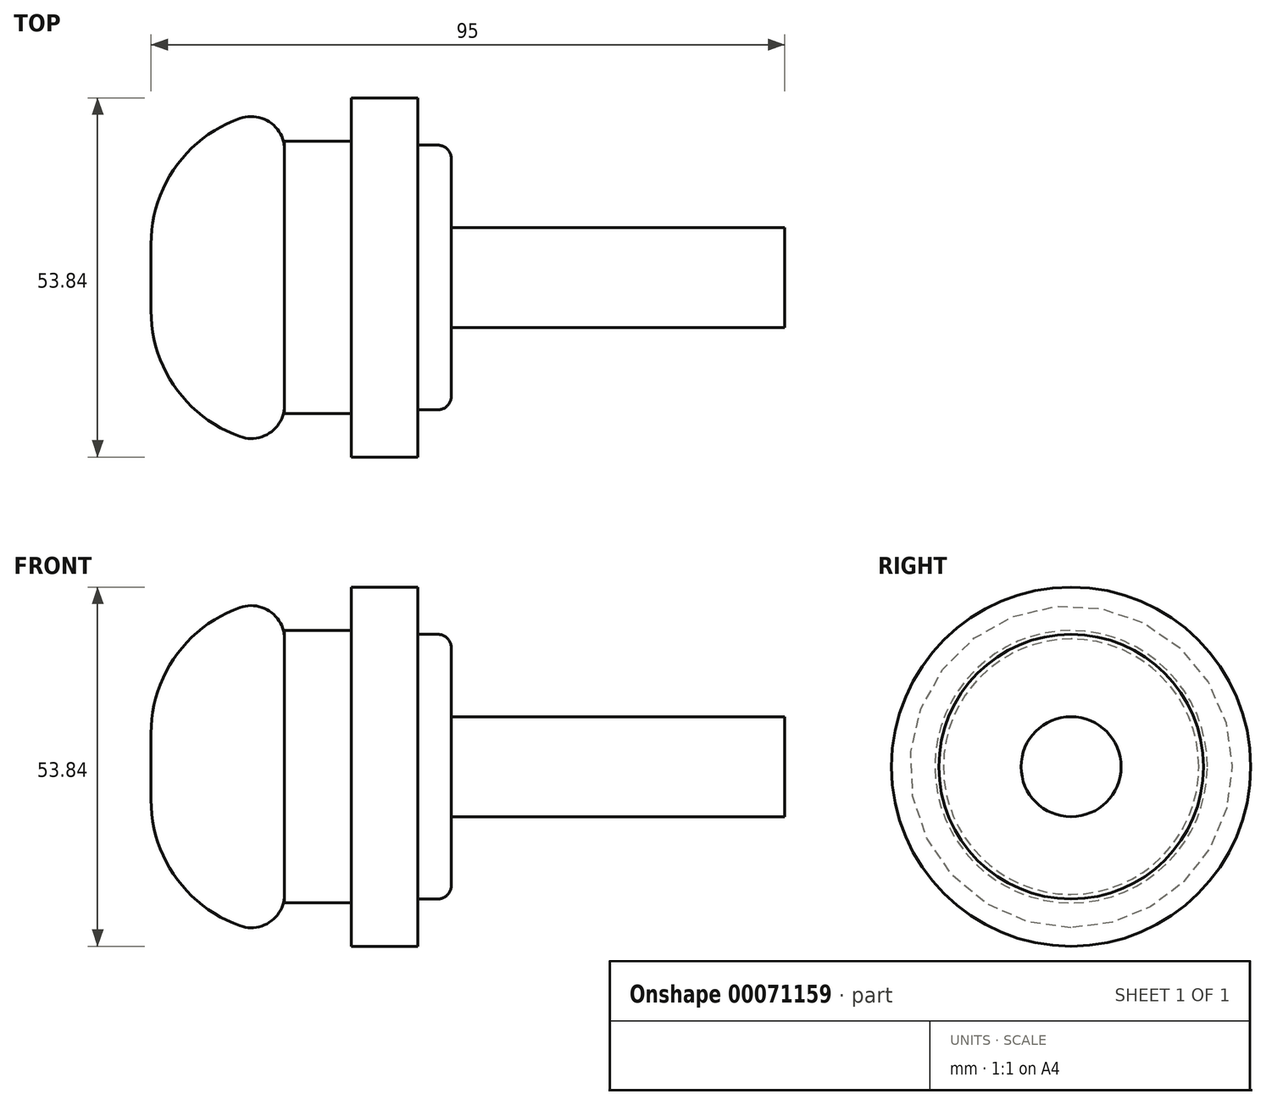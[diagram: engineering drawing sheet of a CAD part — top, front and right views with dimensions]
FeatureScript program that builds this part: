
annotation { "Feature Type Name" : "Feature", "Feature Type Description" : "" }
export const myFeature = defineFeature(function(context is Context, id is Id, definition is map)
    precondition{}
    {
        {
            var Q0;
            Q0=qCreatedBy(makeId("Right.planeOp"),FACE);
            var sketch = newSketch(context, id + "F0", { "sketchPlane" : qUnion([Q0])});
            skCircle(sketch, "E0", {"center": v(0, 0) * mm, "radius": 25 * mm});
            skSolve(sketch);
        }
        {
            var Q0;
            Q0 = qSketchRegion(id + "F0", true);
            extrude(context, id + "F1", {"entities" : qUnion([Q0]), "depth" : 20 * mm});
        }
        {
            var Q0;
            Q0=makeQuery(id+"F1.opExtrude","CAP_EDGE",EDGE,{"disambiguationData":[OSD([sQuery(id+"F0.wireOp",EDGE,"E0")])],"isStart":true});
            fillet(context, id + "F2", {"entities" : qUnion([Q0]), "radius" : 20 * mm, "tangentPropagation" : true, "allowEdgeOverflow" : false});
        }
        {
            var Q0;
            Q0=makeQuery(id+"F1.opExtrude","CAP_FACE",FACE,{"disambiguationData":[OSD([sQuery(id+"F0.wireOp",EDGE,"E0")])],"isStart":false});
            fillet(context, id + "F3", {"entities" : qUnion([Q0]), "radius" : 5 * mm, "tangentPropagation" : true, "allowEdgeOverflow" : false});
        }
        {
            var Q0;
            Q0=makeQuery(id+"F1.opExtrude","CAP_FACE",FACE,{"disambiguationData":[OSD([sQuery(id+"F0.wireOp",EDGE,"E0")])],"isStart":false});
            var sketch = newSketch(context, id + "F4", { "sketchPlane" : qUnion([Q0])});
            skCircle(sketch, "E1", {"center": v(0, 0) * mm, "radius": 20.42 * mm});
            skSolve(sketch);
        }
        {
            var Q0;
            Q0 = qSketchRegion(id + "F4", true);
            extrude(context, id + "F5", {"entities" : qUnion([Q0]), "operationType" : NewBodyOperationType.ADD, "depth" : 10 * mm});
        }
        {
            var Q0;
            Q0=makeQuery(id+"F5.opExtrude","CAP_FACE",FACE,{"disambiguationData":[OSD([sQuery(id+"F4.wireOp",EDGE,"E1")])],"isStart":false});
            var sketch = newSketch(context, id + "F6", { "sketchPlane" : qUnion([Q0])});
            skCircle(sketch, "E2", {"center": v(0, 0) * mm, "radius": 26.92 * mm});
            skSolve(sketch);
        }
        {
            var Q0;
            Q0 = qSketchRegion(id + "F6", true);
            extrude(context, id + "F7", {"entities" : qUnion([Q0]), "operationType" : NewBodyOperationType.ADD, "depth" : 10 * mm});
        }
        {
            var Q0;
            Q0=makeQuery(id+"F7.opExtrude","CAP_FACE",FACE,{"disambiguationData":[OSD([sQuery(id+"F6.wireOp",EDGE,"E2")])],"isStart":false});
            var sketch = newSketch(context, id + "F8", { "sketchPlane" : qUnion([Q0])});
            skCircle(sketch, "E3", {"center": v(0, 0) * mm, "radius": 19.84 * mm});
            skSolve(sketch);
        }
        {
            var Q0;
            Q0=makeQuery(id+"F8.imprint","IMPRINT",FACE,{"disambiguationData":[TD([[makeQuery(id+"F8.imprint","IMPRINT",EDGE,{"derivedFrom":sQuery(id+"F8.wireOp",EDGE,"E3")}),1.0]])]});
            extrude(context, id + "F9", {"entities" : qUnion([Q0]), "operationType" : NewBodyOperationType.ADD, "depth" : 5 * mm});
        }
        {
            var Q0;
            Q0=makeQuery(id+"F9.opExtrude","CAP_EDGE",EDGE,{"disambiguationData":[OSD([sQuery(id+"F8.wireOp",EDGE,"E3")])],"isStart":false});
            fillet(context, id + "F10", {"entities" : qUnion([Q0]), "radius" : 2 * mm, "tangentPropagation" : true, "allowEdgeOverflow" : false});
        }
        {
            var Q0;
            Q0=makeQuery(id+"F9.opExtrude","CAP_FACE",FACE,{"disambiguationData":[OSD([sQuery(id+"F8.wireOp",EDGE,"E3")])],"isStart":false});
            var sketch = newSketch(context, id + "F11", { "sketchPlane" : qUnion([Q0])});
            skCircle(sketch, "E4", {"center": v(0, 0) * mm, "radius": 7.5 * mm});
            skSolve(sketch);
        }
        {
            var Q0;
            Q0=makeQuery(id+"F11.imprint","IMPRINT",FACE,{"disambiguationData":[TD([[makeQuery(id+"F11.imprint","IMPRINT",EDGE,{"derivedFrom":sQuery(id+"F11.wireOp",EDGE,"E4")}),1.0]])]});
            extrude(context, id + "F12", {"entities" : qUnion([Q0]), "operationType" : NewBodyOperationType.ADD, "depth" : 50 * mm});
        }
    });
